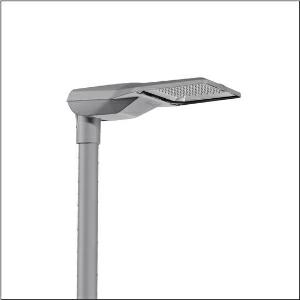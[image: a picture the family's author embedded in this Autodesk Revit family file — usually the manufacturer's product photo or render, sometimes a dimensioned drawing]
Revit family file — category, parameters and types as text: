
# Revit family: streetlight_sl_21_iq_midi___stw1_0a_5xe3e31g08nb_66c1
name_source: partatom
category: Lighting Fixtures
units: mm (PartAtom-declared; Revit-internal decimal feet)

## family parameters
Cut with Voids When Loaded = No
Host = Face
Light Source = No
Part Type = Normal
Room Calculation Point = No
Round Connector Dimension = Use Diameter
Shared = No

## types (1)
- --- (1 x LED, 23230 lm, 155.5 W, 3000K)
    Apparent Load = 155 VA
    CIE Flux Codes = 39 75 98 100 100
    Color Rendering = 70
    Color Temperature = 3000K
    Default Elevation = 1800 mm
    Description = Streetlight SL 21 iQ midi, mast luminaire, primary light control with lens, of PMMA, primary optical cover: cover, of toughened safety glass, transparent, light distribution: STW1.0a, light emission: direct distribution, primary light characteristic: asymmetric, installation type: post-top, side-entry, LED, High Power LED, rated luminous flux: 23.230lm, luminous efficacy: 149lm/W, light colour: 730, colour temperature: 3000K, control: Street-Remote, Auto-Match, Temp-Guard, Lumen-Switch, Night-Set, Smart-Wire, Light-Fading, Desk-Remote (wireless, voltage-free reading and setting of iQ features in the workshop via application-optimized NFC function/RFID function), optimised constant luminous flux control (CLO 2.0), presetting dimming linear, mains connection: 230..240V, AC, 50/60Hz, start of lifetime: 156W, end of service life: 162W, reduction: 69W, luminaire housing, of diecast aluminium, powder-coated, Siteco® metallic grey (DB 702S), corrosivity category C5 mid according to DIN EN ISO 12944, please order mast flange separately, inclination adjustable: 0°, 5°, 10°, 15°, sealing non-destructively replaceable, multi-level sealing system, length: 644mm, width: 335mm, height: 110mm, mast flange for spigot size: 42mm (side-entry): 5XC10008XM4, 60/48mm (side-entry/post-top): 5XC10108XM2, 76/60mm (side-entry/post-top): 5XC10108XM1, protection rating (complete): IP66, insulation class (complete): insulation class II (safety insulation), certification: CE, ENEC, ENEC+, VDE, impact resistance: IK09, permissible operating ambient temperature for outdoor applications: -40..+50°C, standard-compliant lighting for roads and squares, packaging unit: 1 piece

Light Distribution: STW1.0a
    Height = 111 mm
    Lamp = 1 x LED
    Lamp Light Flux = 23230 lm
    Lamp Power = 155.5 W
    Lamp count = 1
    Length = 644 mm
    Luminous efficacy = 149 lm/W
    Manufacturer = Siteco
    ModVariant = No
    Model = 5XE3E31G08NB
    Number of Poles = 1
    OnlyDefault = Yes
    Power Factor = 1
    Product Name = Streetlight SL 21 iQ midi | STW1.0a
    Product group = mast luminaire | pylon top
    ProductGroupID = 6100
    Protection Class = Protection class II
    Protection Degree = IP 66
    RLX_Detail_Level = 1
    RLX_Emergency_Light_Flux = 0 lm
    RLX_Emergency_Type = 0
    RLX_Emergency_Type_DB = No
    RlxData = <blob elided: 91381 chars, md5=4abe3a96>
    Socket = socket
    Standby Power = 0 W
    System Light Flux = 23230 lm
    System Power = 155 W
    Type Comments = factory setting: luminous flux: 100 % | dim-lin: 254 | 823 mA
    Type Image = l_1004298.jpg
    URL = http://relux.com
    VarID = @adj_120317
    Voltage = 0 V
    Weight = 0.00 kg
    Width = 336 mm

## geometry (parser evidence)
native form markers: Blend x4, Sweep x11
no freeform markers — native parametric forms only
